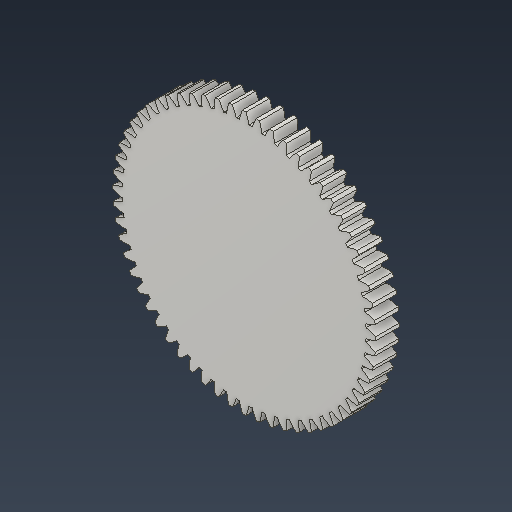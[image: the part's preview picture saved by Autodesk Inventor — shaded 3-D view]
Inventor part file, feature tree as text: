
AUTODESK INVENTOR PART (.ipt)
format: ipt  version: 2021 (Build 250183000, 183)  size: 382,464 bytes
history: native  units: mm (DEFAULTED — no unit token found)
features: plane x3, other x3, sketch x2, extrude x1
ambient origin geometry x8: Origin, YZ Plane, XZ Plane, XY Plane, X Axis, Y Axis, Z Axis, Center Point
bodies: Solid1 (feature_tree)
feature tree (9):
  extrude  "Extrusion1"  Depth=0.5mm TaperAngle=0.0deg
  plane  "Work Plane2"
  plane  "Work Plane8"
  plane  "Work Plane9"
  other  "Engrenagem reta"
  sketch  "Sketch1"  dims[d0=5.575177mm d1=0.5mm d2=0.0mm]
  sketch  "Sketch2"  dims[d3=5.4mm d4=10.0mm d5=0.0mm d16=3.597588mm d17=0.0mm d34=0.523599mm d39=0.0mm d41=0.0mm d43=3.597588mm d46=3.597588mm d47=0.0mm d48=0.0mm]
  other  "Srf1"
  other  "Diâmetro do flanco"
